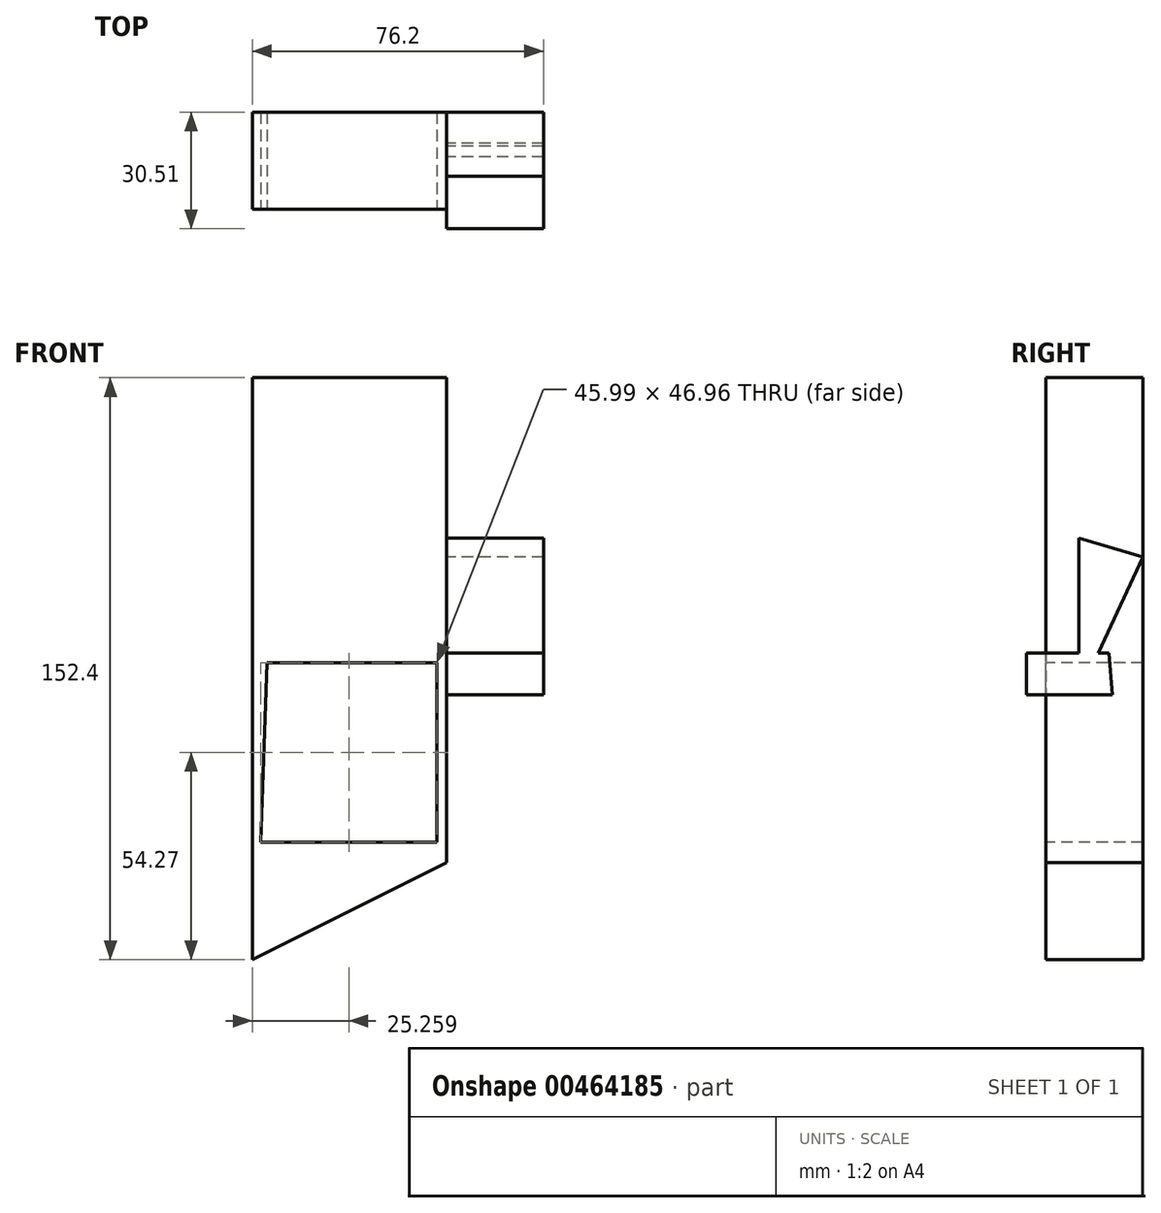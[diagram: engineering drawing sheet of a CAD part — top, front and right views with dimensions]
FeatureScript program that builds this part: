
annotation { "Feature Type Name" : "Feature", "Feature Type Description" : "" }
export const myFeature = defineFeature(function(context is Context, id is Id, definition is map)
    precondition{}
    {
        {
            var Q0;
            Q0=qCreatedBy(makeId("Front.planeOp"),FACE);
            var sketch = newSketch(context, id + "F0", { "sketchPlane" : qUnion([Q0])});
            skLineSegment(sketch, "E0", {"start": v(-43.68, -69.43) * mm, "end": v(-43.68, 82.97) * mm});
            skLineSegment(sketch, "E1", {"start": v(-43.68, 82.97) * mm, "end": v(7.12, 82.97) * mm});
            skLineSegment(sketch, "E2", {"start": v(7.12, 82.97) * mm, "end": v(7.12, -44.03) * mm});
            skLineSegment(sketch, "E3", {"start": v(-43.68, -69.43) * mm, "end": v(7.12, -44.03) * mm});
            skSolve(sketch);
        }
        {
            var Q0;
            Q0=makeQuery(id+"F2.opExtrude","CAP_FACE",FACE,{"disambiguationData":[OSD([sQuery(id+"F0.wireOp",EDGE,"E0"),sQuery(id+"F0.wireOp",EDGE,"E1"),sQuery(id+"F0.wireOp",EDGE,"E2"),sQuery(id+"F0.wireOp",EDGE,"E3")])],"isStart":false});
            var sketch = newSketch(context, id + "F1", { "sketchPlane" : qUnion([Q0])});
            skCircle(sketch, "E4", {"center": v(-25.04, 25.33) * mm, "radius": 5.3 * mm});
            skCircle(sketch, "E5", {"center": v(-10.94, 25.9) * mm, "radius": 5.18 * mm});
            skSolve(sketch);
        }
        {
            var Q0;
            Q0=makeQuery(id+"F0.imprint","IMPRINT",FACE,{"disambiguationData":[TD([[makeQuery(id+"F0.imprint","IMPRINT",EDGE,{"derivedFrom":sQuery(id+"F0.wireOp",EDGE,"E0")}),-1.0]])]});
            extrude(context, id + "F2", {"entities" : qUnion([Q0]), "depth" : 25.4 * mm});
        }
        {
            var Q0;
            Q0=makeQuery(id+"F2.opExtrude","SWEPT_FACE",FACE,{"disambiguationData":[OSD([sQuery(id+"F0.wireOp",EDGE,"E2")])]});
            var sketch = newSketch(context, id + "F3", { "sketchPlane" : qUnion([Q0])});
            skLineSegment(sketch, "E6", {"start": v(-8.92, 10.94) * mm, "end": v(-30.5, 10.94) * mm});
            skLineSegment(sketch, "E7", {"start": v(-30.5, 10.94) * mm, "end": v(-30.5, 0) * mm});
            skLineSegment(sketch, "E8", {"start": v(-30.5, 0) * mm, "end": v(-8.06, 0) * mm});
            skLineSegment(sketch, "E9", {"start": v(-8.06, 0) * mm, "end": v(-8.92, 10.94) * mm});
            skLineSegment(sketch, "E10", {"start": v(-16.8, 0) * mm, "end": v(-16.8, 41.02) * mm});
            skLineSegment(sketch, "E11", {"start": v(-16.8, 41.02) * mm, "end": v(0, 36.05) * mm});
            skLineSegment(sketch, "E12", {"start": v(0, 36.05) * mm, "end": v(-16.8, 0) * mm});
            skSolve(sketch);
        }
        {
            var Q0;
            Q0 = qSketchRegion(id + "F3", true);
            extrude(context, id + "F4", {"entities" : qUnion([Q0]), "operationType" : NewBodyOperationType.ADD, "depth" : 25.4 * mm});
        }
        {
            var Q0;
            Q0=makeQuery(id+"F2.opExtrude","CAP_FACE",FACE,{"disambiguationData":[OSD([sQuery(id+"F0.wireOp",EDGE,"E0"),sQuery(id+"F0.wireOp",EDGE,"E1"),sQuery(id+"F0.wireOp",EDGE,"E2"),sQuery(id+"F0.wireOp",EDGE,"E3")])],"isStart":false});
            var sketch = newSketch(context, id + "F5", { "sketchPlane" : qUnion([Q0])});
            skCircle(sketch, "E13", {"center": v(-34.57, 41.56) * mm, "radius": 6.31 * mm});
            skCircle(sketch, "E14", {"center": v(-8.12, 43.06) * mm, "radius": 5.42 * mm});
            skSolve(sketch);
        }
        {
            var Q0;
            Q0=makeQuery(id+"F5.imprint","IMPRINT",FACE,{"disambiguationData":[TD([[makeQuery(id+"F5.imprint","IMPRINT",EDGE,{"derivedFrom":sQuery(id+"F5.wireOp",EDGE,"E13")}),-1.0]])]});
            var sketch = newSketch(context, id + "F6", { "sketchPlane" : qUnion([Q0])});
            skLineSegment(sketch, "E15", {"start": v(-39.88, 8.32) * mm, "end": v(4.57, 8.32) * mm});
            skLineSegment(sketch, "E16", {"start": v(4.57, 8.32) * mm, "end": v(4.57, -38.64) * mm});
            skLineSegment(sketch, "E17", {"start": v(4.57, -38.64) * mm, "end": v(-41.42, -38.64) * mm});
            skLineSegment(sketch, "E18", {"start": v(-41.42, -38.64) * mm, "end": v(-39.88, 8.32) * mm});
            skSolve(sketch);
        }
        {
            var Q0;
            Q0 = qSketchRegion(id + "F6", true);
            extrude(context, id + "F7", {"entities" : qUnion([Q0]), "operationType" : NewBodyOperationType.REMOVE, "oppositeDirection" : true, "depth" : 50.8 * mm});
        }
    });
